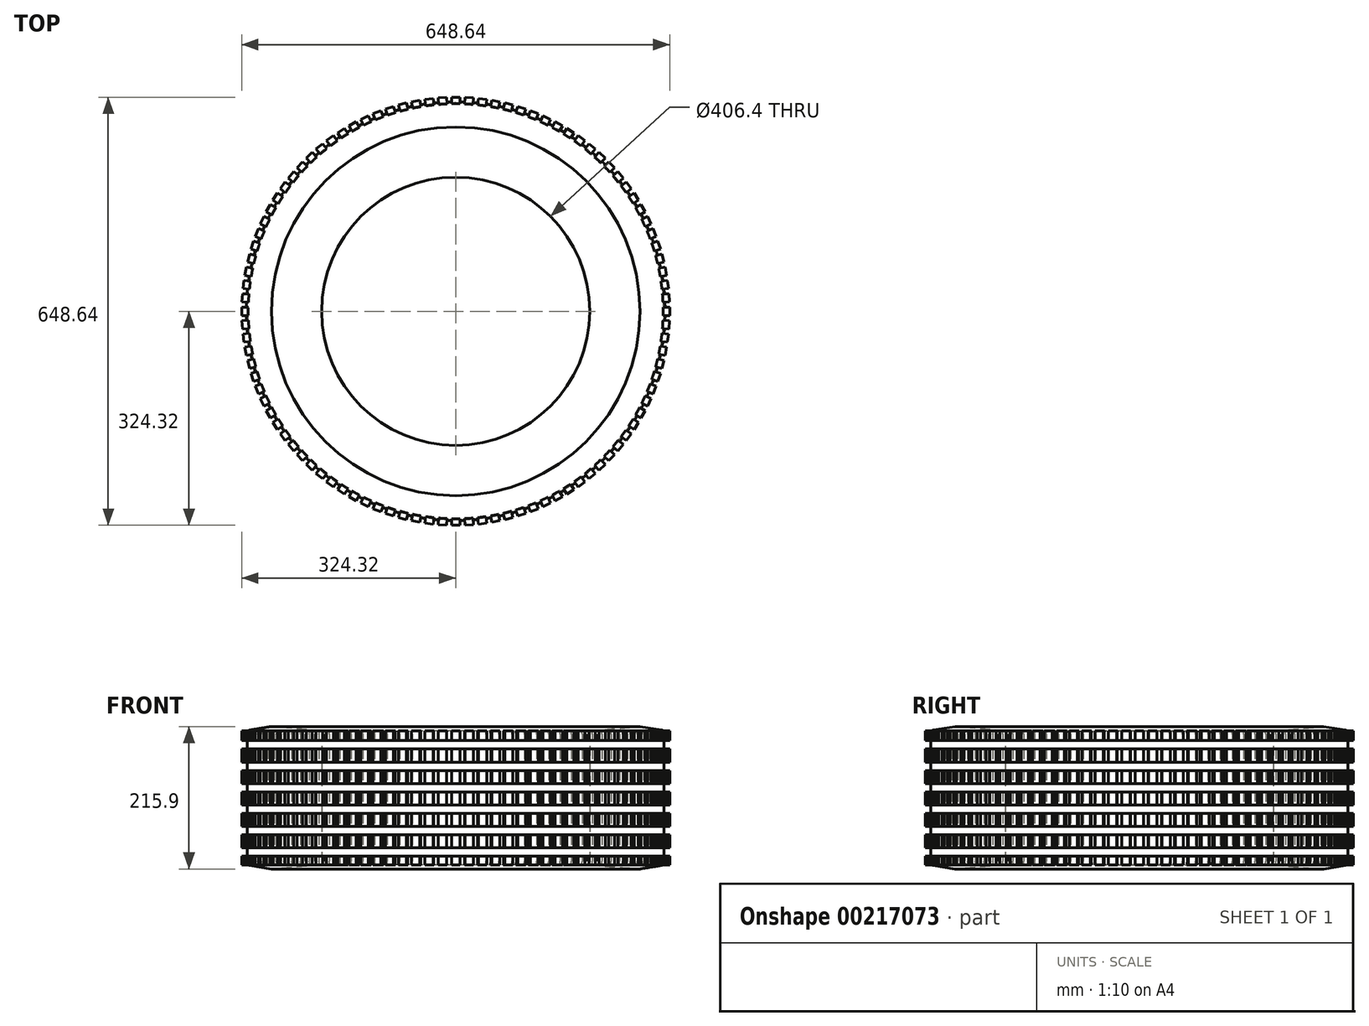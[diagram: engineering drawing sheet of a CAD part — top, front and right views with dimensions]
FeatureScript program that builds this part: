
annotation { "Feature Type Name" : "Feature", "Feature Type Description" : "" }
export const myFeature = defineFeature(function(context is Context, id is Id, definition is map)
    precondition{}
    {
        {
            var Q0;
            Q0=qCreatedBy(makeId("Top.planeOp"),FACE);
            var sketch = newSketch(context, id + "F0", { "sketchPlane" : qUnion([Q0])});
            skCircle(sketch, "E0", {"center": v(0, 0) * mm, "radius": 317.5 * mm});
            skCircle(sketch, "E1", {"center": v(0, 0) * mm, "radius": 203.2 * mm});
            skLineSegment(sketch, "E2", {"start": v(0, 0) * mm, "end": v(0, 317.5) * mm});
            skSolve(sketch);
        }
        {
            var Q0;
            Q0 = qSketchRegion(id + "F0", true);
            extrude(context, id + "F1", {"entities" : qUnion([Q0]), "depth" : 209.55 * mm, "hasSecondDirection" : true, "secondDirectionOppositeDirection" : true, "secondDirectionDepth" : 6.35 * mm});
        }
        {
            var Q0;
            Q0=makeQuery(id+"F1.opExtrude","CAP_EDGE",EDGE,{"disambiguationData":[OSD([sQuery(id+"F0.wireOp",EDGE,"E0")])],"isStart":true});
            chamfer(context, id + "F2", {"entities" : qUnion([Q0]), "chamferType" : ChamferType.TWO_OFFSETS, "width1" : 6.35 * mm, "oppositeDirection" : false, "width2" : 38.1 * mm, "tangentPropagation" : true});
        }
        {
            var Q0;
            Q0=makeQuery(id+"F1.opExtrude","CAP_EDGE",EDGE,{"disambiguationData":[OSD([sQuery(id+"F0.wireOp",EDGE,"E0")])],"isStart":false});
            chamfer(context, id + "F3", {"entities" : qUnion([Q0]), "chamferType" : ChamferType.TWO_OFFSETS, "width1" : 6.35 * mm, "oppositeDirection" : true, "width2" : 38.1 * mm, "tangentPropagation" : true});
        }
        {
            var Q0;
            Q0=makeQuery(id+"F1.opExtrude","CAP_EDGE",EDGE,{"disambiguationData":[OSD([sQuery(id+"F0.wireOp",EDGE,"E1")])],"isStart":true});
            chamfer(context, id + "F4", {"entities" : qUnion([Q0]), "chamferType" : ChamferType.TWO_OFFSETS, "width1" : 76.2 * mm, "oppositeDirection" : false, "width2" : 6.35 * mm, "tangentPropagation" : true});
        }
        {
            var Q0;
            Q0=makeQuery(id+"F1.opExtrude","CAP_EDGE",EDGE,{"disambiguationData":[OSD([sQuery(id+"F0.wireOp",EDGE,"E1")])],"isStart":false});
            chamfer(context, id + "F5", {"entities" : qUnion([Q0]), "chamferType" : ChamferType.TWO_OFFSETS, "width1" : 6.35 * mm, "oppositeDirection" : false, "width2" : 76.2 * mm, "tangentPropagation" : true});
        }
        {
            var Q0;
            {var subQ0=sQuery(id+"F0.wireOp",EDGE,"E0");Q0=makeQuery(id+"F2.opChamfer","BLEND_EDGE",EDGE,{"blendedFrom":[makeQuery(id+"F1.opExtrude","CAP_EDGE",EDGE,{"disambiguationData":[OSD([subQ0])],"isStart":true}),makeQuery(id+"F1.opExtrude","SWEPT_FACE",FACE,{"disambiguationData":[OSD([subQ0])]})],"blendedInto":[makeQuery(id+"F1.opExtrude","SWEPT_FACE",FACE,{"disambiguationData":[OSD([subQ0])]})]});}
            var Q1;
            {var subQ0=sQuery(id+"F0.wireOp",EDGE,"E0");Q1=makeQuery(id+"F3.opChamfer","BLEND_EDGE",EDGE,{"blendedFrom":[makeQuery(id+"F1.opExtrude","CAP_EDGE",EDGE,{"disambiguationData":[OSD([subQ0])],"isStart":false}),makeQuery(id+"F1.opExtrude","SWEPT_FACE",FACE,{"disambiguationData":[OSD([subQ0])]})],"blendedInto":[makeQuery(id+"F1.opExtrude","SWEPT_FACE",FACE,{"disambiguationData":[OSD([subQ0])]})]});}
            fillet(context, id + "F6", {"entities" : qUnion([Q0, Q1]), "radius" : 6.35 * mm, "tangentPropagation" : true, "allowEdgeOverflow" : false});
        }
        {
            var Q0;
            Q0=qCreatedBy(makeId("Top.planeOp"),FACE);
            var sketch = newSketch(context, id + "F7", { "sketchPlane" : qUnion([Q0])});
            skLineSegment(sketch, "E3.bottom", {"start": v(6.35, -311.62) * mm, "end": v(-6.35, -311.62) * mm});
            skLineSegment(sketch, "E3.top", {"start": v(6.35, -324.32) * mm, "end": v(-6.35, -324.32) * mm});
            skLineSegment(sketch, "E3.left", {"start": v(6.35, -311.62) * mm, "end": v(6.35, -324.32) * mm});
            skLineSegment(sketch, "E3.right", {"start": v(-6.35, -311.62) * mm, "end": v(-6.35, -324.32) * mm});
            skPoint(sketch, "E3.middle", {"position": v(0, -317.97) * mm});
            skLineSegment(sketch, "E4.1.0", {"start": v(13.23, -311.4) * mm, "end": v(14.03, -324.08) * mm});
            skLineSegment(sketch, "E4.1.1", {"start": v(25.9, -310.61) * mm, "end": v(26.7, -323.29) * mm});
            skLineSegment(sketch, "E4.1.2", {"start": v(26.7, -323.29) * mm, "end": v(14.03, -324.08) * mm});
            skLineSegment(sketch, "E4.1.3", {"start": v(25.9, -310.61) * mm, "end": v(13.23, -311.4) * mm});
            skLineSegment(sketch, "E4.2.0", {"start": v(32.76, -309.96) * mm, "end": v(34.35, -322.56) * mm});
            skLineSegment(sketch, "E4.2.1", {"start": v(45.36, -308.37) * mm, "end": v(46.95, -320.97) * mm});
            skLineSegment(sketch, "E4.2.2", {"start": v(46.95, -320.97) * mm, "end": v(34.35, -322.56) * mm});
            skLineSegment(sketch, "E4.2.3", {"start": v(45.36, -308.37) * mm, "end": v(32.76, -309.96) * mm});
            skLineSegment(sketch, "E4.3.0", {"start": v(52.15, -307.3) * mm, "end": v(54.53, -319.77) * mm});
            skLineSegment(sketch, "E4.3.1", {"start": v(64.63, -304.91) * mm, "end": v(67, -317.39) * mm});
            skLineSegment(sketch, "E4.3.2", {"start": v(67, -317.39) * mm, "end": v(54.53, -319.77) * mm});
            skLineSegment(sketch, "E4.3.3", {"start": v(64.63, -304.91) * mm, "end": v(52.15, -307.3) * mm});
            skLineSegment(sketch, "E4.4.0", {"start": v(71.35, -303.41) * mm, "end": v(74.5, -315.71) * mm});
            skLineSegment(sketch, "E4.4.1", {"start": v(83.65, -300.25) * mm, "end": v(86.8, -312.56) * mm});
            skLineSegment(sketch, "E4.4.2", {"start": v(86.8, -312.56) * mm, "end": v(74.5, -315.71) * mm});
            skLineSegment(sketch, "E4.4.3", {"start": v(83.65, -300.25) * mm, "end": v(71.35, -303.41) * mm});
            skLineSegment(sketch, "E4.5.0", {"start": v(90.26, -298.33) * mm, "end": v(94.18, -310.41) * mm});
            skLineSegment(sketch, "E4.5.1", {"start": v(102.34, -294.4) * mm, "end": v(106.26, -306.49) * mm});
            skLineSegment(sketch, "E4.5.2", {"start": v(106.26, -306.49) * mm, "end": v(94.18, -310.41) * mm});
            skLineSegment(sketch, "E4.5.3", {"start": v(102.34, -294.4) * mm, "end": v(90.26, -298.33) * mm});
            skLineSegment(sketch, "E4.6.0", {"start": v(108.81, -292.08) * mm, "end": v(113.49, -303.89) * mm});
            skLineSegment(sketch, "E4.6.1", {"start": v(120.62, -287.4) * mm, "end": v(125.3, -299.21) * mm});
            skLineSegment(sketch, "E4.6.2", {"start": v(125.3, -299.21) * mm, "end": v(113.49, -303.89) * mm});
            skLineSegment(sketch, "E4.6.3", {"start": v(120.62, -287.4) * mm, "end": v(108.81, -292.08) * mm});
            skLineSegment(sketch, "E4.7.0", {"start": v(126.94, -284.67) * mm, "end": v(132.34, -296.16) * mm});
            skLineSegment(sketch, "E4.7.1", {"start": v(138.43, -279.26) * mm, "end": v(143.84, -290.75) * mm});
            skLineSegment(sketch, "E4.7.2", {"start": v(143.84, -290.75) * mm, "end": v(132.34, -296.16) * mm});
            skLineSegment(sketch, "E4.7.3", {"start": v(138.43, -279.26) * mm, "end": v(126.94, -284.67) * mm});
            skLineSegment(sketch, "E4.8.0", {"start": v(144.56, -276.14) * mm, "end": v(150.68, -287.27) * mm});
            skLineSegment(sketch, "E4.8.1", {"start": v(155.7, -270.02) * mm, "end": v(161.8, -281.15) * mm});
            skLineSegment(sketch, "E4.8.2", {"start": v(161.8, -281.15) * mm, "end": v(150.68, -287.27) * mm});
            skLineSegment(sketch, "E4.8.3", {"start": v(155.7, -270.02) * mm, "end": v(144.56, -276.14) * mm});
            skLineSegment(sketch, "E4.9.0", {"start": v(161.61, -266.52) * mm, "end": v(168.42, -277.24) * mm});
            skLineSegment(sketch, "E4.9.1", {"start": v(172.34, -259.71) * mm, "end": v(179.14, -270.43) * mm});
            skLineSegment(sketch, "E4.9.2", {"start": v(179.14, -270.43) * mm, "end": v(168.42, -277.24) * mm});
            skLineSegment(sketch, "E4.9.3", {"start": v(172.34, -259.71) * mm, "end": v(161.61, -266.52) * mm});
            skLineSegment(sketch, "E4.10.0", {"start": v(178.03, -255.84) * mm, "end": v(185.5, -266.12) * mm});
            skLineSegment(sketch, "E4.10.1", {"start": v(188.3, -248.38) * mm, "end": v(195.77, -258.65) * mm});
            skLineSegment(sketch, "E4.10.2", {"start": v(195.77, -258.65) * mm, "end": v(185.5, -266.12) * mm});
            skLineSegment(sketch, "E4.10.3", {"start": v(188.3, -248.38) * mm, "end": v(178.03, -255.84) * mm});
            skLineSegment(sketch, "E4.11.0", {"start": v(193.74, -244.16) * mm, "end": v(201.84, -253.94) * mm});
            skLineSegment(sketch, "E4.11.1", {"start": v(203.53, -236.06) * mm, "end": v(211.62, -245.85) * mm});
            skLineSegment(sketch, "E4.11.2", {"start": v(211.62, -245.85) * mm, "end": v(201.84, -253.94) * mm});
            skLineSegment(sketch, "E4.11.3", {"start": v(203.53, -236.06) * mm, "end": v(193.74, -244.16) * mm});
            skLineSegment(sketch, "E4.12.0", {"start": v(208.7, -231.51) * mm, "end": v(217.39, -240.77) * mm});
            skLineSegment(sketch, "E4.12.1", {"start": v(217.95, -222.82) * mm, "end": v(226.64, -232.08) * mm});
            skLineSegment(sketch, "E4.12.2", {"start": v(226.64, -232.08) * mm, "end": v(217.39, -240.77) * mm});
            skLineSegment(sketch, "E4.12.3", {"start": v(217.95, -222.82) * mm, "end": v(208.7, -231.51) * mm});
            skLineSegment(sketch, "E4.13.0", {"start": v(222.82, -217.95) * mm, "end": v(232.08, -226.64) * mm});
            skLineSegment(sketch, "E4.13.1", {"start": v(231.51, -208.7) * mm, "end": v(240.77, -217.39) * mm});
            skLineSegment(sketch, "E4.13.2", {"start": v(240.77, -217.39) * mm, "end": v(232.08, -226.64) * mm});
            skLineSegment(sketch, "E4.13.3", {"start": v(231.51, -208.7) * mm, "end": v(222.82, -217.95) * mm});
            skLineSegment(sketch, "E4.14.0", {"start": v(236.06, -203.53) * mm, "end": v(245.85, -211.62) * mm});
            skLineSegment(sketch, "E4.14.1", {"start": v(244.16, -193.74) * mm, "end": v(253.94, -201.84) * mm});
            skLineSegment(sketch, "E4.14.2", {"start": v(253.94, -201.84) * mm, "end": v(245.85, -211.62) * mm});
            skLineSegment(sketch, "E4.14.3", {"start": v(244.16, -193.74) * mm, "end": v(236.06, -203.53) * mm});
            skLineSegment(sketch, "E4.15.0", {"start": v(248.38, -188.3) * mm, "end": v(258.65, -195.77) * mm});
            skLineSegment(sketch, "E4.15.1", {"start": v(255.84, -178.03) * mm, "end": v(266.12, -185.5) * mm});
            skLineSegment(sketch, "E4.15.2", {"start": v(266.12, -185.5) * mm, "end": v(258.65, -195.77) * mm});
            skLineSegment(sketch, "E4.15.3", {"start": v(255.84, -178.03) * mm, "end": v(248.38, -188.3) * mm});
            skLineSegment(sketch, "E4.16.0", {"start": v(259.71, -172.34) * mm, "end": v(270.43, -179.14) * mm});
            skLineSegment(sketch, "E4.16.1", {"start": v(266.52, -161.61) * mm, "end": v(277.24, -168.42) * mm});
            skLineSegment(sketch, "E4.16.2", {"start": v(277.24, -168.42) * mm, "end": v(270.43, -179.14) * mm});
            skLineSegment(sketch, "E4.16.3", {"start": v(266.52, -161.61) * mm, "end": v(259.71, -172.34) * mm});
            skLineSegment(sketch, "E4.17.0", {"start": v(270.02, -155.7) * mm, "end": v(281.15, -161.8) * mm});
            skLineSegment(sketch, "E4.17.1", {"start": v(276.14, -144.56) * mm, "end": v(287.27, -150.68) * mm});
            skLineSegment(sketch, "E4.17.2", {"start": v(287.27, -150.68) * mm, "end": v(281.15, -161.8) * mm});
            skLineSegment(sketch, "E4.17.3", {"start": v(276.14, -144.56) * mm, "end": v(270.02, -155.7) * mm});
            skLineSegment(sketch, "E4.18.0", {"start": v(279.26, -138.43) * mm, "end": v(290.75, -143.84) * mm});
            skLineSegment(sketch, "E4.18.1", {"start": v(284.67, -126.94) * mm, "end": v(296.16, -132.34) * mm});
            skLineSegment(sketch, "E4.18.2", {"start": v(296.16, -132.34) * mm, "end": v(290.75, -143.84) * mm});
            skLineSegment(sketch, "E4.18.3", {"start": v(284.67, -126.94) * mm, "end": v(279.26, -138.43) * mm});
            skLineSegment(sketch, "E4.19.0", {"start": v(287.4, -120.62) * mm, "end": v(299.21, -125.3) * mm});
            skLineSegment(sketch, "E4.19.1", {"start": v(292.08, -108.81) * mm, "end": v(303.89, -113.49) * mm});
            skLineSegment(sketch, "E4.19.2", {"start": v(303.89, -113.49) * mm, "end": v(299.21, -125.3) * mm});
            skLineSegment(sketch, "E4.19.3", {"start": v(292.08, -108.81) * mm, "end": v(287.4, -120.62) * mm});
            skLineSegment(sketch, "E4.20.0", {"start": v(294.4, -102.34) * mm, "end": v(306.49, -106.26) * mm});
            skLineSegment(sketch, "E4.20.1", {"start": v(298.33, -90.26) * mm, "end": v(310.41, -94.18) * mm});
            skLineSegment(sketch, "E4.20.2", {"start": v(310.41, -94.18) * mm, "end": v(306.49, -106.26) * mm});
            skLineSegment(sketch, "E4.20.3", {"start": v(298.33, -90.26) * mm, "end": v(294.4, -102.34) * mm});
            skLineSegment(sketch, "E4.21.0", {"start": v(300.25, -83.65) * mm, "end": v(312.56, -86.8) * mm});
            skLineSegment(sketch, "E4.21.1", {"start": v(303.41, -71.35) * mm, "end": v(315.71, -74.5) * mm});
            skLineSegment(sketch, "E4.21.2", {"start": v(315.71, -74.5) * mm, "end": v(312.56, -86.8) * mm});
            skLineSegment(sketch, "E4.21.3", {"start": v(303.41, -71.35) * mm, "end": v(300.25, -83.65) * mm});
            skLineSegment(sketch, "E4.22.0", {"start": v(304.91, -64.63) * mm, "end": v(317.39, -67) * mm});
            skLineSegment(sketch, "E4.22.1", {"start": v(307.3, -52.15) * mm, "end": v(319.77, -54.53) * mm});
            skLineSegment(sketch, "E4.22.2", {"start": v(319.77, -54.53) * mm, "end": v(317.39, -67) * mm});
            skLineSegment(sketch, "E4.22.3", {"start": v(307.3, -52.15) * mm, "end": v(304.91, -64.63) * mm});
            skLineSegment(sketch, "E4.23.0", {"start": v(308.37, -45.36) * mm, "end": v(320.97, -46.95) * mm});
            skLineSegment(sketch, "E4.23.1", {"start": v(309.96, -32.76) * mm, "end": v(322.56, -34.35) * mm});
            skLineSegment(sketch, "E4.23.2", {"start": v(322.56, -34.35) * mm, "end": v(320.97, -46.95) * mm});
            skLineSegment(sketch, "E4.23.3", {"start": v(309.96, -32.76) * mm, "end": v(308.37, -45.36) * mm});
            skLineSegment(sketch, "E4.24.0", {"start": v(310.61, -25.9) * mm, "end": v(323.29, -26.7) * mm});
            skLineSegment(sketch, "E4.24.1", {"start": v(311.4, -13.23) * mm, "end": v(324.08, -14.03) * mm});
            skLineSegment(sketch, "E4.24.2", {"start": v(324.08, -14.03) * mm, "end": v(323.29, -26.7) * mm});
            skLineSegment(sketch, "E4.24.3", {"start": v(311.4, -13.23) * mm, "end": v(310.61, -25.9) * mm});
            skLineSegment(sketch, "E4.25.0", {"start": v(311.62, -6.35) * mm, "end": v(324.32, -6.35) * mm});
            skLineSegment(sketch, "E4.25.1", {"start": v(311.62, 6.35) * mm, "end": v(324.32, 6.35) * mm});
            skLineSegment(sketch, "E4.25.2", {"start": v(324.32, 6.35) * mm, "end": v(324.32, -6.35) * mm});
            skLineSegment(sketch, "E4.25.3", {"start": v(311.62, 6.35) * mm, "end": v(311.62, -6.35) * mm});
            skLineSegment(sketch, "E4.26.0", {"start": v(311.4, 13.23) * mm, "end": v(324.08, 14.03) * mm});
            skLineSegment(sketch, "E4.26.1", {"start": v(310.61, 25.9) * mm, "end": v(323.29, 26.7) * mm});
            skLineSegment(sketch, "E4.26.2", {"start": v(323.29, 26.7) * mm, "end": v(324.08, 14.03) * mm});
            skLineSegment(sketch, "E4.26.3", {"start": v(310.61, 25.9) * mm, "end": v(311.4, 13.23) * mm});
            skLineSegment(sketch, "E4.27.0", {"start": v(309.96, 32.76) * mm, "end": v(322.56, 34.35) * mm});
            skLineSegment(sketch, "E4.27.1", {"start": v(308.37, 45.36) * mm, "end": v(320.97, 46.95) * mm});
            skLineSegment(sketch, "E4.27.2", {"start": v(320.97, 46.95) * mm, "end": v(322.56, 34.35) * mm});
            skLineSegment(sketch, "E4.27.3", {"start": v(308.37, 45.36) * mm, "end": v(309.96, 32.76) * mm});
            skLineSegment(sketch, "E4.28.0", {"start": v(307.3, 52.15) * mm, "end": v(319.77, 54.53) * mm});
            skLineSegment(sketch, "E4.28.1", {"start": v(304.91, 64.63) * mm, "end": v(317.39, 67) * mm});
            skLineSegment(sketch, "E4.28.2", {"start": v(317.39, 67) * mm, "end": v(319.77, 54.53) * mm});
            skLineSegment(sketch, "E4.28.3", {"start": v(304.91, 64.63) * mm, "end": v(307.3, 52.15) * mm});
            skLineSegment(sketch, "E4.29.0", {"start": v(303.41, 71.35) * mm, "end": v(315.71, 74.5) * mm});
            skLineSegment(sketch, "E4.29.1", {"start": v(300.25, 83.65) * mm, "end": v(312.56, 86.8) * mm});
            skLineSegment(sketch, "E4.29.2", {"start": v(312.56, 86.8) * mm, "end": v(315.71, 74.5) * mm});
            skLineSegment(sketch, "E4.29.3", {"start": v(300.25, 83.65) * mm, "end": v(303.41, 71.35) * mm});
            skLineSegment(sketch, "E4.30.0", {"start": v(298.33, 90.26) * mm, "end": v(310.41, 94.18) * mm});
            skLineSegment(sketch, "E4.30.1", {"start": v(294.4, 102.34) * mm, "end": v(306.49, 106.26) * mm});
            skLineSegment(sketch, "E4.30.2", {"start": v(306.49, 106.26) * mm, "end": v(310.41, 94.18) * mm});
            skLineSegment(sketch, "E4.30.3", {"start": v(294.4, 102.34) * mm, "end": v(298.33, 90.26) * mm});
            skLineSegment(sketch, "E4.31.0", {"start": v(292.08, 108.81) * mm, "end": v(303.89, 113.49) * mm});
            skLineSegment(sketch, "E4.31.1", {"start": v(287.4, 120.62) * mm, "end": v(299.21, 125.3) * mm});
            skLineSegment(sketch, "E4.31.2", {"start": v(299.21, 125.3) * mm, "end": v(303.89, 113.49) * mm});
            skLineSegment(sketch, "E4.31.3", {"start": v(287.4, 120.62) * mm, "end": v(292.08, 108.81) * mm});
            skLineSegment(sketch, "E4.32.0", {"start": v(284.67, 126.94) * mm, "end": v(296.16, 132.34) * mm});
            skLineSegment(sketch, "E4.32.1", {"start": v(279.26, 138.43) * mm, "end": v(290.75, 143.84) * mm});
            skLineSegment(sketch, "E4.32.2", {"start": v(290.75, 143.84) * mm, "end": v(296.16, 132.34) * mm});
            skLineSegment(sketch, "E4.32.3", {"start": v(279.26, 138.43) * mm, "end": v(284.67, 126.94) * mm});
            skLineSegment(sketch, "E4.33.0", {"start": v(276.14, 144.56) * mm, "end": v(287.27, 150.68) * mm});
            skLineSegment(sketch, "E4.33.1", {"start": v(270.02, 155.7) * mm, "end": v(281.15, 161.8) * mm});
            skLineSegment(sketch, "E4.33.2", {"start": v(281.15, 161.8) * mm, "end": v(287.27, 150.68) * mm});
            skLineSegment(sketch, "E4.33.3", {"start": v(270.02, 155.7) * mm, "end": v(276.14, 144.56) * mm});
            skLineSegment(sketch, "E4.34.0", {"start": v(266.52, 161.61) * mm, "end": v(277.24, 168.42) * mm});
            skLineSegment(sketch, "E4.34.1", {"start": v(259.71, 172.34) * mm, "end": v(270.43, 179.14) * mm});
            skLineSegment(sketch, "E4.34.2", {"start": v(270.43, 179.14) * mm, "end": v(277.24, 168.42) * mm});
            skLineSegment(sketch, "E4.34.3", {"start": v(259.71, 172.34) * mm, "end": v(266.52, 161.61) * mm});
            skLineSegment(sketch, "E4.35.0", {"start": v(255.84, 178.03) * mm, "end": v(266.12, 185.5) * mm});
            skLineSegment(sketch, "E4.35.1", {"start": v(248.38, 188.3) * mm, "end": v(258.65, 195.77) * mm});
            skLineSegment(sketch, "E4.35.2", {"start": v(258.65, 195.77) * mm, "end": v(266.12, 185.5) * mm});
            skLineSegment(sketch, "E4.35.3", {"start": v(248.38, 188.3) * mm, "end": v(255.84, 178.03) * mm});
            skLineSegment(sketch, "E4.36.0", {"start": v(244.16, 193.74) * mm, "end": v(253.94, 201.84) * mm});
            skLineSegment(sketch, "E4.36.1", {"start": v(236.06, 203.53) * mm, "end": v(245.85, 211.62) * mm});
            skLineSegment(sketch, "E4.36.2", {"start": v(245.85, 211.62) * mm, "end": v(253.94, 201.84) * mm});
            skLineSegment(sketch, "E4.36.3", {"start": v(236.06, 203.53) * mm, "end": v(244.16, 193.74) * mm});
            skLineSegment(sketch, "E4.37.0", {"start": v(231.51, 208.7) * mm, "end": v(240.77, 217.39) * mm});
            skLineSegment(sketch, "E4.37.1", {"start": v(222.82, 217.95) * mm, "end": v(232.08, 226.64) * mm});
            skLineSegment(sketch, "E4.37.2", {"start": v(232.08, 226.64) * mm, "end": v(240.77, 217.39) * mm});
            skLineSegment(sketch, "E4.37.3", {"start": v(222.82, 217.95) * mm, "end": v(231.51, 208.7) * mm});
            skLineSegment(sketch, "E4.38.0", {"start": v(217.95, 222.82) * mm, "end": v(226.64, 232.08) * mm});
            skLineSegment(sketch, "E4.38.1", {"start": v(208.7, 231.51) * mm, "end": v(217.39, 240.77) * mm});
            skLineSegment(sketch, "E4.38.2", {"start": v(217.39, 240.77) * mm, "end": v(226.64, 232.08) * mm});
            skLineSegment(sketch, "E4.38.3", {"start": v(208.7, 231.51) * mm, "end": v(217.95, 222.82) * mm});
            skLineSegment(sketch, "E4.39.0", {"start": v(203.53, 236.06) * mm, "end": v(211.62, 245.85) * mm});
            skLineSegment(sketch, "E4.39.1", {"start": v(193.74, 244.16) * mm, "end": v(201.84, 253.94) * mm});
            skLineSegment(sketch, "E4.39.2", {"start": v(201.84, 253.94) * mm, "end": v(211.62, 245.85) * mm});
            skLineSegment(sketch, "E4.39.3", {"start": v(193.74, 244.16) * mm, "end": v(203.53, 236.06) * mm});
            skLineSegment(sketch, "E4.40.0", {"start": v(188.3, 248.38) * mm, "end": v(195.77, 258.65) * mm});
            skLineSegment(sketch, "E4.40.1", {"start": v(178.03, 255.84) * mm, "end": v(185.5, 266.12) * mm});
            skLineSegment(sketch, "E4.40.2", {"start": v(185.5, 266.12) * mm, "end": v(195.77, 258.65) * mm});
            skLineSegment(sketch, "E4.40.3", {"start": v(178.03, 255.84) * mm, "end": v(188.3, 248.38) * mm});
            skLineSegment(sketch, "E4.41.0", {"start": v(172.34, 259.71) * mm, "end": v(179.14, 270.43) * mm});
            skLineSegment(sketch, "E4.41.1", {"start": v(161.61, 266.52) * mm, "end": v(168.42, 277.24) * mm});
            skLineSegment(sketch, "E4.41.2", {"start": v(168.42, 277.24) * mm, "end": v(179.14, 270.43) * mm});
            skLineSegment(sketch, "E4.41.3", {"start": v(161.61, 266.52) * mm, "end": v(172.34, 259.71) * mm});
            skLineSegment(sketch, "E4.42.0", {"start": v(155.7, 270.02) * mm, "end": v(161.8, 281.15) * mm});
            skLineSegment(sketch, "E4.42.1", {"start": v(144.56, 276.14) * mm, "end": v(150.68, 287.27) * mm});
            skLineSegment(sketch, "E4.42.2", {"start": v(150.68, 287.27) * mm, "end": v(161.8, 281.15) * mm});
            skLineSegment(sketch, "E4.42.3", {"start": v(144.56, 276.14) * mm, "end": v(155.7, 270.02) * mm});
            skLineSegment(sketch, "E4.43.0", {"start": v(138.43, 279.26) * mm, "end": v(143.84, 290.75) * mm});
            skLineSegment(sketch, "E4.43.1", {"start": v(126.94, 284.67) * mm, "end": v(132.34, 296.16) * mm});
            skLineSegment(sketch, "E4.43.2", {"start": v(132.34, 296.16) * mm, "end": v(143.84, 290.75) * mm});
            skLineSegment(sketch, "E4.43.3", {"start": v(126.94, 284.67) * mm, "end": v(138.43, 279.26) * mm});
            skLineSegment(sketch, "E4.44.0", {"start": v(120.62, 287.4) * mm, "end": v(125.3, 299.21) * mm});
            skLineSegment(sketch, "E4.44.1", {"start": v(108.81, 292.08) * mm, "end": v(113.49, 303.89) * mm});
            skLineSegment(sketch, "E4.44.2", {"start": v(113.49, 303.89) * mm, "end": v(125.3, 299.21) * mm});
            skLineSegment(sketch, "E4.44.3", {"start": v(108.81, 292.08) * mm, "end": v(120.62, 287.4) * mm});
            skLineSegment(sketch, "E4.45.0", {"start": v(102.34, 294.4) * mm, "end": v(106.26, 306.49) * mm});
            skLineSegment(sketch, "E4.45.1", {"start": v(90.26, 298.33) * mm, "end": v(94.18, 310.41) * mm});
            skLineSegment(sketch, "E4.45.2", {"start": v(94.18, 310.41) * mm, "end": v(106.26, 306.49) * mm});
            skLineSegment(sketch, "E4.45.3", {"start": v(90.26, 298.33) * mm, "end": v(102.34, 294.4) * mm});
            skLineSegment(sketch, "E4.46.0", {"start": v(83.65, 300.25) * mm, "end": v(86.8, 312.56) * mm});
            skLineSegment(sketch, "E4.46.1", {"start": v(71.35, 303.41) * mm, "end": v(74.5, 315.71) * mm});
            skLineSegment(sketch, "E4.46.2", {"start": v(74.5, 315.71) * mm, "end": v(86.8, 312.56) * mm});
            skLineSegment(sketch, "E4.46.3", {"start": v(71.35, 303.41) * mm, "end": v(83.65, 300.25) * mm});
            skLineSegment(sketch, "E4.47.0", {"start": v(64.63, 304.91) * mm, "end": v(67, 317.39) * mm});
            skLineSegment(sketch, "E4.47.1", {"start": v(52.15, 307.3) * mm, "end": v(54.53, 319.77) * mm});
            skLineSegment(sketch, "E4.47.2", {"start": v(54.53, 319.77) * mm, "end": v(67, 317.39) * mm});
            skLineSegment(sketch, "E4.47.3", {"start": v(52.15, 307.3) * mm, "end": v(64.63, 304.91) * mm});
            skLineSegment(sketch, "E4.48.0", {"start": v(45.36, 308.37) * mm, "end": v(46.95, 320.97) * mm});
            skLineSegment(sketch, "E4.48.1", {"start": v(32.76, 309.96) * mm, "end": v(34.35, 322.56) * mm});
            skLineSegment(sketch, "E4.48.2", {"start": v(34.35, 322.56) * mm, "end": v(46.95, 320.97) * mm});
            skLineSegment(sketch, "E4.48.3", {"start": v(32.76, 309.96) * mm, "end": v(45.36, 308.37) * mm});
            skLineSegment(sketch, "E4.49.0", {"start": v(25.9, 310.61) * mm, "end": v(26.7, 323.29) * mm});
            skLineSegment(sketch, "E4.49.1", {"start": v(13.23, 311.4) * mm, "end": v(14.03, 324.08) * mm});
            skLineSegment(sketch, "E4.49.2", {"start": v(14.03, 324.08) * mm, "end": v(26.7, 323.29) * mm});
            skLineSegment(sketch, "E4.49.3", {"start": v(13.23, 311.4) * mm, "end": v(25.9, 310.61) * mm});
            skLineSegment(sketch, "E4.50.0", {"start": v(6.35, 311.62) * mm, "end": v(6.35, 324.32) * mm});
            skLineSegment(sketch, "E4.50.1", {"start": v(-6.35, 311.62) * mm, "end": v(-6.35, 324.32) * mm});
            skLineSegment(sketch, "E4.50.2", {"start": v(-6.35, 324.32) * mm, "end": v(6.35, 324.32) * mm});
            skLineSegment(sketch, "E4.50.3", {"start": v(-6.35, 311.62) * mm, "end": v(6.35, 311.62) * mm});
            skLineSegment(sketch, "E4.51.0", {"start": v(-13.23, 311.4) * mm, "end": v(-14.03, 324.08) * mm});
            skLineSegment(sketch, "E4.51.1", {"start": v(-25.9, 310.61) * mm, "end": v(-26.7, 323.29) * mm});
            skLineSegment(sketch, "E4.51.2", {"start": v(-26.7, 323.29) * mm, "end": v(-14.03, 324.08) * mm});
            skLineSegment(sketch, "E4.51.3", {"start": v(-25.9, 310.61) * mm, "end": v(-13.23, 311.4) * mm});
            skLineSegment(sketch, "E4.52.0", {"start": v(-32.76, 309.96) * mm, "end": v(-34.35, 322.56) * mm});
            skLineSegment(sketch, "E4.52.1", {"start": v(-45.36, 308.37) * mm, "end": v(-46.95, 320.97) * mm});
            skLineSegment(sketch, "E4.52.2", {"start": v(-46.95, 320.97) * mm, "end": v(-34.35, 322.56) * mm});
            skLineSegment(sketch, "E4.52.3", {"start": v(-45.36, 308.37) * mm, "end": v(-32.76, 309.96) * mm});
            skLineSegment(sketch, "E4.53.0", {"start": v(-52.15, 307.3) * mm, "end": v(-54.53, 319.77) * mm});
            skLineSegment(sketch, "E4.53.1", {"start": v(-64.63, 304.91) * mm, "end": v(-67, 317.39) * mm});
            skLineSegment(sketch, "E4.53.2", {"start": v(-67, 317.39) * mm, "end": v(-54.53, 319.77) * mm});
            skLineSegment(sketch, "E4.53.3", {"start": v(-64.63, 304.91) * mm, "end": v(-52.15, 307.3) * mm});
            skLineSegment(sketch, "E4.54.0", {"start": v(-71.35, 303.41) * mm, "end": v(-74.5, 315.71) * mm});
            skLineSegment(sketch, "E4.54.1", {"start": v(-83.65, 300.25) * mm, "end": v(-86.8, 312.56) * mm});
            skLineSegment(sketch, "E4.54.2", {"start": v(-86.8, 312.56) * mm, "end": v(-74.5, 315.71) * mm});
            skLineSegment(sketch, "E4.54.3", {"start": v(-83.65, 300.25) * mm, "end": v(-71.35, 303.41) * mm});
            skLineSegment(sketch, "E4.55.0", {"start": v(-90.26, 298.33) * mm, "end": v(-94.18, 310.41) * mm});
            skLineSegment(sketch, "E4.55.1", {"start": v(-102.34, 294.4) * mm, "end": v(-106.26, 306.49) * mm});
            skLineSegment(sketch, "E4.55.2", {"start": v(-106.26, 306.49) * mm, "end": v(-94.18, 310.41) * mm});
            skLineSegment(sketch, "E4.55.3", {"start": v(-102.34, 294.4) * mm, "end": v(-90.26, 298.33) * mm});
            skLineSegment(sketch, "E4.56.0", {"start": v(-108.81, 292.08) * mm, "end": v(-113.49, 303.89) * mm});
            skLineSegment(sketch, "E4.56.1", {"start": v(-120.62, 287.4) * mm, "end": v(-125.3, 299.21) * mm});
            skLineSegment(sketch, "E4.56.2", {"start": v(-125.3, 299.21) * mm, "end": v(-113.49, 303.89) * mm});
            skLineSegment(sketch, "E4.56.3", {"start": v(-120.62, 287.4) * mm, "end": v(-108.81, 292.08) * mm});
            skLineSegment(sketch, "E4.57.0", {"start": v(-126.94, 284.67) * mm, "end": v(-132.34, 296.16) * mm});
            skLineSegment(sketch, "E4.57.1", {"start": v(-138.43, 279.26) * mm, "end": v(-143.84, 290.75) * mm});
            skLineSegment(sketch, "E4.57.2", {"start": v(-143.84, 290.75) * mm, "end": v(-132.34, 296.16) * mm});
            skLineSegment(sketch, "E4.57.3", {"start": v(-138.43, 279.26) * mm, "end": v(-126.94, 284.67) * mm});
            skLineSegment(sketch, "E4.58.0", {"start": v(-144.56, 276.14) * mm, "end": v(-150.68, 287.27) * mm});
            skLineSegment(sketch, "E4.58.1", {"start": v(-155.7, 270.02) * mm, "end": v(-161.8, 281.15) * mm});
            skLineSegment(sketch, "E4.58.2", {"start": v(-161.8, 281.15) * mm, "end": v(-150.68, 287.27) * mm});
            skLineSegment(sketch, "E4.58.3", {"start": v(-155.7, 270.02) * mm, "end": v(-144.56, 276.14) * mm});
            skLineSegment(sketch, "E4.59.0", {"start": v(-161.61, 266.52) * mm, "end": v(-168.42, 277.24) * mm});
            skLineSegment(sketch, "E4.59.1", {"start": v(-172.34, 259.71) * mm, "end": v(-179.14, 270.43) * mm});
            skLineSegment(sketch, "E4.59.2", {"start": v(-179.14, 270.43) * mm, "end": v(-168.42, 277.24) * mm});
            skLineSegment(sketch, "E4.59.3", {"start": v(-172.34, 259.71) * mm, "end": v(-161.61, 266.52) * mm});
            skLineSegment(sketch, "E4.60.0", {"start": v(-178.03, 255.84) * mm, "end": v(-185.5, 266.12) * mm});
            skLineSegment(sketch, "E4.60.1", {"start": v(-188.3, 248.38) * mm, "end": v(-195.77, 258.65) * mm});
            skLineSegment(sketch, "E4.60.2", {"start": v(-195.77, 258.65) * mm, "end": v(-185.5, 266.12) * mm});
            skLineSegment(sketch, "E4.60.3", {"start": v(-188.3, 248.38) * mm, "end": v(-178.03, 255.84) * mm});
            skLineSegment(sketch, "E4.61.0", {"start": v(-193.74, 244.16) * mm, "end": v(-201.84, 253.94) * mm});
            skLineSegment(sketch, "E4.61.1", {"start": v(-203.53, 236.06) * mm, "end": v(-211.62, 245.85) * mm});
            skLineSegment(sketch, "E4.61.2", {"start": v(-211.62, 245.85) * mm, "end": v(-201.84, 253.94) * mm});
            skLineSegment(sketch, "E4.61.3", {"start": v(-203.53, 236.06) * mm, "end": v(-193.74, 244.16) * mm});
            skLineSegment(sketch, "E4.62.0", {"start": v(-208.7, 231.51) * mm, "end": v(-217.39, 240.77) * mm});
            skLineSegment(sketch, "E4.62.1", {"start": v(-217.95, 222.82) * mm, "end": v(-226.64, 232.08) * mm});
            skLineSegment(sketch, "E4.62.2", {"start": v(-226.64, 232.08) * mm, "end": v(-217.39, 240.77) * mm});
            skLineSegment(sketch, "E4.62.3", {"start": v(-217.95, 222.82) * mm, "end": v(-208.7, 231.51) * mm});
            skLineSegment(sketch, "E4.63.0", {"start": v(-222.82, 217.95) * mm, "end": v(-232.08, 226.64) * mm});
            skLineSegment(sketch, "E4.63.1", {"start": v(-231.51, 208.7) * mm, "end": v(-240.77, 217.39) * mm});
            skLineSegment(sketch, "E4.63.2", {"start": v(-240.77, 217.39) * mm, "end": v(-232.08, 226.64) * mm});
            skLineSegment(sketch, "E4.63.3", {"start": v(-231.51, 208.7) * mm, "end": v(-222.82, 217.95) * mm});
            skLineSegment(sketch, "E4.64.0", {"start": v(-236.06, 203.53) * mm, "end": v(-245.85, 211.62) * mm});
            skLineSegment(sketch, "E4.64.1", {"start": v(-244.16, 193.74) * mm, "end": v(-253.94, 201.84) * mm});
            skLineSegment(sketch, "E4.64.2", {"start": v(-253.94, 201.84) * mm, "end": v(-245.85, 211.62) * mm});
            skLineSegment(sketch, "E4.64.3", {"start": v(-244.16, 193.74) * mm, "end": v(-236.06, 203.53) * mm});
            skLineSegment(sketch, "E4.65.0", {"start": v(-248.38, 188.3) * mm, "end": v(-258.65, 195.77) * mm});
            skLineSegment(sketch, "E4.65.1", {"start": v(-255.84, 178.03) * mm, "end": v(-266.12, 185.5) * mm});
            skLineSegment(sketch, "E4.65.2", {"start": v(-266.12, 185.5) * mm, "end": v(-258.65, 195.77) * mm});
            skLineSegment(sketch, "E4.65.3", {"start": v(-255.84, 178.03) * mm, "end": v(-248.38, 188.3) * mm});
            skLineSegment(sketch, "E4.66.0", {"start": v(-259.71, 172.34) * mm, "end": v(-270.43, 179.14) * mm});
            skLineSegment(sketch, "E4.66.1", {"start": v(-266.52, 161.61) * mm, "end": v(-277.24, 168.42) * mm});
            skLineSegment(sketch, "E4.66.2", {"start": v(-277.24, 168.42) * mm, "end": v(-270.43, 179.14) * mm});
            skLineSegment(sketch, "E4.66.3", {"start": v(-266.52, 161.61) * mm, "end": v(-259.71, 172.34) * mm});
            skLineSegment(sketch, "E4.67.0", {"start": v(-270.02, 155.7) * mm, "end": v(-281.15, 161.8) * mm});
            skLineSegment(sketch, "E4.67.1", {"start": v(-276.14, 144.56) * mm, "end": v(-287.27, 150.68) * mm});
            skLineSegment(sketch, "E4.67.2", {"start": v(-287.27, 150.68) * mm, "end": v(-281.15, 161.8) * mm});
            skLineSegment(sketch, "E4.67.3", {"start": v(-276.14, 144.56) * mm, "end": v(-270.02, 155.7) * mm});
            skLineSegment(sketch, "E4.68.0", {"start": v(-279.26, 138.43) * mm, "end": v(-290.75, 143.84) * mm});
            skLineSegment(sketch, "E4.68.1", {"start": v(-284.67, 126.94) * mm, "end": v(-296.16, 132.34) * mm});
            skLineSegment(sketch, "E4.68.2", {"start": v(-296.16, 132.34) * mm, "end": v(-290.75, 143.84) * mm});
            skLineSegment(sketch, "E4.68.3", {"start": v(-284.67, 126.94) * mm, "end": v(-279.26, 138.43) * mm});
            skLineSegment(sketch, "E4.69.0", {"start": v(-287.4, 120.62) * mm, "end": v(-299.21, 125.3) * mm});
            skLineSegment(sketch, "E4.69.1", {"start": v(-292.08, 108.81) * mm, "end": v(-303.89, 113.49) * mm});
            skLineSegment(sketch, "E4.69.2", {"start": v(-303.89, 113.49) * mm, "end": v(-299.21, 125.3) * mm});
            skLineSegment(sketch, "E4.69.3", {"start": v(-292.08, 108.81) * mm, "end": v(-287.4, 120.62) * mm});
            skLineSegment(sketch, "E4.70.0", {"start": v(-294.4, 102.34) * mm, "end": v(-306.49, 106.26) * mm});
            skLineSegment(sketch, "E4.70.1", {"start": v(-298.33, 90.26) * mm, "end": v(-310.41, 94.18) * mm});
            skLineSegment(sketch, "E4.70.2", {"start": v(-310.41, 94.18) * mm, "end": v(-306.49, 106.26) * mm});
            skLineSegment(sketch, "E4.70.3", {"start": v(-298.33, 90.26) * mm, "end": v(-294.4, 102.34) * mm});
            skLineSegment(sketch, "E4.71.0", {"start": v(-300.25, 83.65) * mm, "end": v(-312.56, 86.8) * mm});
            skLineSegment(sketch, "E4.71.1", {"start": v(-303.41, 71.35) * mm, "end": v(-315.71, 74.5) * mm});
            skLineSegment(sketch, "E4.71.2", {"start": v(-315.71, 74.5) * mm, "end": v(-312.56, 86.8) * mm});
            skLineSegment(sketch, "E4.71.3", {"start": v(-303.41, 71.35) * mm, "end": v(-300.25, 83.65) * mm});
            skLineSegment(sketch, "E4.72.0", {"start": v(-304.91, 64.63) * mm, "end": v(-317.39, 67) * mm});
            skLineSegment(sketch, "E4.72.1", {"start": v(-307.3, 52.15) * mm, "end": v(-319.77, 54.53) * mm});
            skLineSegment(sketch, "E4.72.2", {"start": v(-319.77, 54.53) * mm, "end": v(-317.39, 67) * mm});
            skLineSegment(sketch, "E4.72.3", {"start": v(-307.3, 52.15) * mm, "end": v(-304.91, 64.63) * mm});
            skLineSegment(sketch, "E4.73.0", {"start": v(-308.37, 45.36) * mm, "end": v(-320.97, 46.95) * mm});
            skLineSegment(sketch, "E4.73.1", {"start": v(-309.96, 32.76) * mm, "end": v(-322.56, 34.35) * mm});
            skLineSegment(sketch, "E4.73.2", {"start": v(-322.56, 34.35) * mm, "end": v(-320.97, 46.95) * mm});
            skLineSegment(sketch, "E4.73.3", {"start": v(-309.96, 32.76) * mm, "end": v(-308.37, 45.36) * mm});
            skLineSegment(sketch, "E4.74.0", {"start": v(-310.61, 25.9) * mm, "end": v(-323.29, 26.7) * mm});
            skLineSegment(sketch, "E4.74.1", {"start": v(-311.4, 13.23) * mm, "end": v(-324.08, 14.03) * mm});
            skLineSegment(sketch, "E4.74.2", {"start": v(-324.08, 14.03) * mm, "end": v(-323.29, 26.7) * mm});
            skLineSegment(sketch, "E4.74.3", {"start": v(-311.4, 13.23) * mm, "end": v(-310.61, 25.9) * mm});
            skLineSegment(sketch, "E4.75.0", {"start": v(-311.62, 6.35) * mm, "end": v(-324.32, 6.35) * mm});
            skLineSegment(sketch, "E4.75.1", {"start": v(-311.62, -6.35) * mm, "end": v(-324.32, -6.35) * mm});
            skLineSegment(sketch, "E4.75.2", {"start": v(-324.32, -6.35) * mm, "end": v(-324.32, 6.35) * mm});
            skLineSegment(sketch, "E4.75.3", {"start": v(-311.62, -6.35) * mm, "end": v(-311.62, 6.35) * mm});
            skLineSegment(sketch, "E4.76.0", {"start": v(-311.4, -13.23) * mm, "end": v(-324.08, -14.03) * mm});
            skLineSegment(sketch, "E4.76.1", {"start": v(-310.61, -25.9) * mm, "end": v(-323.29, -26.7) * mm});
            skLineSegment(sketch, "E4.76.2", {"start": v(-323.29, -26.7) * mm, "end": v(-324.08, -14.03) * mm});
            skLineSegment(sketch, "E4.76.3", {"start": v(-310.61, -25.9) * mm, "end": v(-311.4, -13.23) * mm});
            skLineSegment(sketch, "E4.77.0", {"start": v(-309.96, -32.76) * mm, "end": v(-322.56, -34.35) * mm});
            skLineSegment(sketch, "E4.77.1", {"start": v(-308.37, -45.36) * mm, "end": v(-320.97, -46.95) * mm});
            skLineSegment(sketch, "E4.77.2", {"start": v(-320.97, -46.95) * mm, "end": v(-322.56, -34.35) * mm});
            skLineSegment(sketch, "E4.77.3", {"start": v(-308.37, -45.36) * mm, "end": v(-309.96, -32.76) * mm});
            skLineSegment(sketch, "E4.78.0", {"start": v(-307.3, -52.15) * mm, "end": v(-319.77, -54.53) * mm});
            skLineSegment(sketch, "E4.78.1", {"start": v(-304.91, -64.63) * mm, "end": v(-317.39, -67) * mm});
            skLineSegment(sketch, "E4.78.2", {"start": v(-317.39, -67) * mm, "end": v(-319.77, -54.53) * mm});
            skLineSegment(sketch, "E4.78.3", {"start": v(-304.91, -64.63) * mm, "end": v(-307.3, -52.15) * mm});
            skLineSegment(sketch, "E4.79.0", {"start": v(-303.41, -71.35) * mm, "end": v(-315.71, -74.5) * mm});
            skLineSegment(sketch, "E4.79.1", {"start": v(-300.25, -83.65) * mm, "end": v(-312.56, -86.8) * mm});
            skLineSegment(sketch, "E4.79.2", {"start": v(-312.56, -86.8) * mm, "end": v(-315.71, -74.5) * mm});
            skLineSegment(sketch, "E4.79.3", {"start": v(-300.25, -83.65) * mm, "end": v(-303.41, -71.35) * mm});
            skLineSegment(sketch, "E4.80.0", {"start": v(-298.33, -90.26) * mm, "end": v(-310.41, -94.18) * mm});
            skLineSegment(sketch, "E4.80.1", {"start": v(-294.4, -102.34) * mm, "end": v(-306.49, -106.26) * mm});
            skLineSegment(sketch, "E4.80.2", {"start": v(-306.49, -106.26) * mm, "end": v(-310.41, -94.18) * mm});
            skLineSegment(sketch, "E4.80.3", {"start": v(-294.4, -102.34) * mm, "end": v(-298.33, -90.26) * mm});
            skLineSegment(sketch, "E4.81.0", {"start": v(-292.08, -108.81) * mm, "end": v(-303.89, -113.49) * mm});
            skLineSegment(sketch, "E4.81.1", {"start": v(-287.4, -120.62) * mm, "end": v(-299.21, -125.3) * mm});
            skLineSegment(sketch, "E4.81.2", {"start": v(-299.21, -125.3) * mm, "end": v(-303.89, -113.49) * mm});
            skLineSegment(sketch, "E4.81.3", {"start": v(-287.4, -120.62) * mm, "end": v(-292.08, -108.81) * mm});
            skLineSegment(sketch, "E4.82.0", {"start": v(-284.67, -126.94) * mm, "end": v(-296.16, -132.34) * mm});
            skLineSegment(sketch, "E4.82.1", {"start": v(-279.26, -138.43) * mm, "end": v(-290.75, -143.84) * mm});
            skLineSegment(sketch, "E4.82.2", {"start": v(-290.75, -143.84) * mm, "end": v(-296.16, -132.34) * mm});
            skLineSegment(sketch, "E4.82.3", {"start": v(-279.26, -138.43) * mm, "end": v(-284.67, -126.94) * mm});
            skLineSegment(sketch, "E4.83.0", {"start": v(-276.14, -144.56) * mm, "end": v(-287.27, -150.68) * mm});
            skLineSegment(sketch, "E4.83.1", {"start": v(-270.02, -155.7) * mm, "end": v(-281.15, -161.8) * mm});
            skLineSegment(sketch, "E4.83.2", {"start": v(-281.15, -161.8) * mm, "end": v(-287.27, -150.68) * mm});
            skLineSegment(sketch, "E4.83.3", {"start": v(-270.02, -155.7) * mm, "end": v(-276.14, -144.56) * mm});
            skLineSegment(sketch, "E4.84.0", {"start": v(-266.52, -161.61) * mm, "end": v(-277.24, -168.42) * mm});
            skLineSegment(sketch, "E4.84.1", {"start": v(-259.71, -172.34) * mm, "end": v(-270.43, -179.14) * mm});
            skLineSegment(sketch, "E4.84.2", {"start": v(-270.43, -179.14) * mm, "end": v(-277.24, -168.42) * mm});
            skLineSegment(sketch, "E4.84.3", {"start": v(-259.71, -172.34) * mm, "end": v(-266.52, -161.61) * mm});
            skLineSegment(sketch, "E4.85.0", {"start": v(-255.84, -178.03) * mm, "end": v(-266.12, -185.5) * mm});
            skLineSegment(sketch, "E4.85.1", {"start": v(-248.38, -188.3) * mm, "end": v(-258.65, -195.77) * mm});
            skLineSegment(sketch, "E4.85.2", {"start": v(-258.65, -195.77) * mm, "end": v(-266.12, -185.5) * mm});
            skLineSegment(sketch, "E4.85.3", {"start": v(-248.38, -188.3) * mm, "end": v(-255.84, -178.03) * mm});
            skLineSegment(sketch, "E4.86.0", {"start": v(-244.16, -193.74) * mm, "end": v(-253.94, -201.84) * mm});
            skLineSegment(sketch, "E4.86.1", {"start": v(-236.06, -203.53) * mm, "end": v(-245.85, -211.62) * mm});
            skLineSegment(sketch, "E4.86.2", {"start": v(-245.85, -211.62) * mm, "end": v(-253.94, -201.84) * mm});
            skLineSegment(sketch, "E4.86.3", {"start": v(-236.06, -203.53) * mm, "end": v(-244.16, -193.74) * mm});
            skLineSegment(sketch, "E4.87.0", {"start": v(-231.51, -208.7) * mm, "end": v(-240.77, -217.39) * mm});
            skLineSegment(sketch, "E4.87.1", {"start": v(-222.82, -217.95) * mm, "end": v(-232.08, -226.64) * mm});
            skLineSegment(sketch, "E4.87.2", {"start": v(-232.08, -226.64) * mm, "end": v(-240.77, -217.39) * mm});
            skLineSegment(sketch, "E4.87.3", {"start": v(-222.82, -217.95) * mm, "end": v(-231.51, -208.7) * mm});
            skLineSegment(sketch, "E4.88.0", {"start": v(-217.95, -222.82) * mm, "end": v(-226.64, -232.08) * mm});
            skLineSegment(sketch, "E4.88.1", {"start": v(-208.7, -231.51) * mm, "end": v(-217.39, -240.77) * mm});
            skLineSegment(sketch, "E4.88.2", {"start": v(-217.39, -240.77) * mm, "end": v(-226.64, -232.08) * mm});
            skLineSegment(sketch, "E4.88.3", {"start": v(-208.7, -231.51) * mm, "end": v(-217.95, -222.82) * mm});
            skLineSegment(sketch, "E4.89.0", {"start": v(-203.53, -236.06) * mm, "end": v(-211.62, -245.85) * mm});
            skLineSegment(sketch, "E4.89.1", {"start": v(-193.74, -244.16) * mm, "end": v(-201.84, -253.94) * mm});
            skLineSegment(sketch, "E4.89.2", {"start": v(-201.84, -253.94) * mm, "end": v(-211.62, -245.85) * mm});
            skLineSegment(sketch, "E4.89.3", {"start": v(-193.74, -244.16) * mm, "end": v(-203.53, -236.06) * mm});
            skLineSegment(sketch, "E4.90.0", {"start": v(-188.3, -248.38) * mm, "end": v(-195.77, -258.65) * mm});
            skLineSegment(sketch, "E4.90.1", {"start": v(-178.03, -255.84) * mm, "end": v(-185.5, -266.12) * mm});
            skLineSegment(sketch, "E4.90.2", {"start": v(-185.5, -266.12) * mm, "end": v(-195.77, -258.65) * mm});
            skLineSegment(sketch, "E4.90.3", {"start": v(-178.03, -255.84) * mm, "end": v(-188.3, -248.38) * mm});
            skLineSegment(sketch, "E4.91.0", {"start": v(-172.34, -259.71) * mm, "end": v(-179.14, -270.43) * mm});
            skLineSegment(sketch, "E4.91.1", {"start": v(-161.61, -266.52) * mm, "end": v(-168.42, -277.24) * mm});
            skLineSegment(sketch, "E4.91.2", {"start": v(-168.42, -277.24) * mm, "end": v(-179.14, -270.43) * mm});
            skLineSegment(sketch, "E4.91.3", {"start": v(-161.61, -266.52) * mm, "end": v(-172.34, -259.71) * mm});
            skLineSegment(sketch, "E4.92.0", {"start": v(-155.7, -270.02) * mm, "end": v(-161.8, -281.15) * mm});
            skLineSegment(sketch, "E4.92.1", {"start": v(-144.56, -276.14) * mm, "end": v(-150.68, -287.27) * mm});
            skLineSegment(sketch, "E4.92.2", {"start": v(-150.68, -287.27) * mm, "end": v(-161.8, -281.15) * mm});
            skLineSegment(sketch, "E4.92.3", {"start": v(-144.56, -276.14) * mm, "end": v(-155.7, -270.02) * mm});
            skLineSegment(sketch, "E4.93.0", {"start": v(-138.43, -279.26) * mm, "end": v(-143.84, -290.75) * mm});
            skLineSegment(sketch, "E4.93.1", {"start": v(-126.94, -284.67) * mm, "end": v(-132.34, -296.16) * mm});
            skLineSegment(sketch, "E4.93.2", {"start": v(-132.34, -296.16) * mm, "end": v(-143.84, -290.75) * mm});
            skLineSegment(sketch, "E4.93.3", {"start": v(-126.94, -284.67) * mm, "end": v(-138.43, -279.26) * mm});
            skLineSegment(sketch, "E4.94.0", {"start": v(-120.62, -287.4) * mm, "end": v(-125.3, -299.21) * mm});
            skLineSegment(sketch, "E4.94.1", {"start": v(-108.81, -292.08) * mm, "end": v(-113.49, -303.89) * mm});
            skLineSegment(sketch, "E4.94.2", {"start": v(-113.49, -303.89) * mm, "end": v(-125.3, -299.21) * mm});
            skLineSegment(sketch, "E4.94.3", {"start": v(-108.81, -292.08) * mm, "end": v(-120.62, -287.4) * mm});
            skLineSegment(sketch, "E4.95.0", {"start": v(-102.34, -294.4) * mm, "end": v(-106.26, -306.49) * mm});
            skLineSegment(sketch, "E4.95.1", {"start": v(-90.26, -298.33) * mm, "end": v(-94.18, -310.41) * mm});
            skLineSegment(sketch, "E4.95.2", {"start": v(-94.18, -310.41) * mm, "end": v(-106.26, -306.49) * mm});
            skLineSegment(sketch, "E4.95.3", {"start": v(-90.26, -298.33) * mm, "end": v(-102.34, -294.4) * mm});
            skLineSegment(sketch, "E4.96.0", {"start": v(-83.65, -300.25) * mm, "end": v(-86.8, -312.56) * mm});
            skLineSegment(sketch, "E4.96.1", {"start": v(-71.35, -303.41) * mm, "end": v(-74.5, -315.71) * mm});
            skLineSegment(sketch, "E4.96.2", {"start": v(-74.5, -315.71) * mm, "end": v(-86.8, -312.56) * mm});
            skLineSegment(sketch, "E4.96.3", {"start": v(-71.35, -303.41) * mm, "end": v(-83.65, -300.25) * mm});
            skLineSegment(sketch, "E4.97.0", {"start": v(-64.63, -304.91) * mm, "end": v(-67, -317.39) * mm});
            skLineSegment(sketch, "E4.97.1", {"start": v(-52.15, -307.3) * mm, "end": v(-54.53, -319.77) * mm});
            skLineSegment(sketch, "E4.97.2", {"start": v(-54.53, -319.77) * mm, "end": v(-67, -317.39) * mm});
            skLineSegment(sketch, "E4.97.3", {"start": v(-52.15, -307.3) * mm, "end": v(-64.63, -304.91) * mm});
            skLineSegment(sketch, "E4.98.0", {"start": v(-45.36, -308.37) * mm, "end": v(-46.95, -320.97) * mm});
            skLineSegment(sketch, "E4.98.1", {"start": v(-32.76, -309.96) * mm, "end": v(-34.35, -322.56) * mm});
            skLineSegment(sketch, "E4.98.2", {"start": v(-34.35, -322.56) * mm, "end": v(-46.95, -320.97) * mm});
            skLineSegment(sketch, "E4.98.3", {"start": v(-32.76, -309.96) * mm, "end": v(-45.36, -308.37) * mm});
            skLineSegment(sketch, "E4.99.0", {"start": v(-25.9, -310.61) * mm, "end": v(-26.7, -323.29) * mm});
            skLineSegment(sketch, "E4.99.1", {"start": v(-13.23, -311.4) * mm, "end": v(-14.03, -324.08) * mm});
            skLineSegment(sketch, "E4.99.2", {"start": v(-14.03, -324.08) * mm, "end": v(-26.7, -323.29) * mm});
            skLineSegment(sketch, "E4.99.3", {"start": v(-13.23, -311.4) * mm, "end": v(-25.9, -310.61) * mm});
            skPoint(sketch, "E4.center", {"position": v(0, 0) * mm});
            skSolve(sketch);
        }
        {
            var Q0;
            Q0 = qSketchRegion(id + "F7", true);
            extrude(context, id + "F8", {"entities" : qUnion([Q0]), "operationType" : NewBodyOperationType.ADD, "depth" : 203.2 * mm});
        }
        {
            var Q0;
            Q0=qCreatedBy(makeId("Right.planeOp"),FACE);
            var sketch = newSketch(context, id + "F9", { "sketchPlane" : qUnion([Q0])});
            skLineSegment(sketch, "E5.bottom", {"start": v(316.02, 12.83) * mm, "end": v(328.72, 12.83) * mm});
            skLineSegment(sketch, "E5.top", {"start": v(316.02, 25.53) * mm, "end": v(328.72, 25.53) * mm});
            skLineSegment(sketch, "E5.left", {"start": v(316.02, 12.83) * mm, "end": v(316.02, 25.53) * mm});
            skLineSegment(sketch, "E5.right", {"start": v(328.72, 12.83) * mm, "end": v(328.72, 25.53) * mm});
            skPoint(sketch, "E5.middle", {"position": v(322.37, 19.18) * mm});
            skLineSegment(sketch, "E6.0.1.0", {"start": v(316.02, 45.34) * mm, "end": v(328.72, 45.34) * mm});
            skLineSegment(sketch, "E6.0.1.1", {"start": v(328.72, 45.34) * mm, "end": v(328.72, 58.04) * mm});
            skLineSegment(sketch, "E6.0.1.2", {"start": v(316.02, 58.04) * mm, "end": v(328.72, 58.04) * mm});
            skLineSegment(sketch, "E6.0.1.3", {"start": v(316.02, 45.34) * mm, "end": v(316.02, 58.04) * mm});
            skLineSegment(sketch, "E6.0.2.0", {"start": v(316.02, 77.86) * mm, "end": v(328.72, 77.86) * mm});
            skLineSegment(sketch, "E6.0.2.1", {"start": v(328.72, 77.86) * mm, "end": v(328.72, 90.56) * mm});
            skLineSegment(sketch, "E6.0.2.2", {"start": v(316.02, 90.56) * mm, "end": v(328.72, 90.56) * mm});
            skLineSegment(sketch, "E6.0.2.3", {"start": v(316.02, 77.86) * mm, "end": v(316.02, 90.56) * mm});
            skLineSegment(sketch, "E6.0.3.0", {"start": v(316.02, 110.37) * mm, "end": v(328.72, 110.37) * mm});
            skLineSegment(sketch, "E6.0.3.1", {"start": v(328.72, 110.37) * mm, "end": v(328.72, 123.07) * mm});
            skLineSegment(sketch, "E6.0.3.2", {"start": v(316.02, 123.07) * mm, "end": v(328.72, 123.07) * mm});
            skLineSegment(sketch, "E6.0.3.3", {"start": v(316.02, 110.37) * mm, "end": v(316.02, 123.07) * mm});
            skLineSegment(sketch, "E6.0.4.0", {"start": v(316.02, 142.88) * mm, "end": v(328.72, 142.88) * mm});
            skLineSegment(sketch, "E6.0.4.1", {"start": v(328.72, 142.88) * mm, "end": v(328.72, 155.58) * mm});
            skLineSegment(sketch, "E6.0.4.2", {"start": v(316.02, 155.58) * mm, "end": v(328.72, 155.58) * mm});
            skLineSegment(sketch, "E6.0.4.3", {"start": v(316.02, 142.88) * mm, "end": v(316.02, 155.58) * mm});
            skLineSegment(sketch, "E6.0.5.0", {"start": v(316.02, 175.4) * mm, "end": v(328.72, 175.4) * mm});
            skLineSegment(sketch, "E6.0.5.1", {"start": v(328.72, 175.4) * mm, "end": v(328.72, 188.1) * mm});
            skLineSegment(sketch, "E6.0.5.2", {"start": v(316.02, 188.1) * mm, "end": v(328.72, 188.1) * mm});
            skLineSegment(sketch, "E6.0.5.3", {"start": v(316.02, 175.4) * mm, "end": v(316.02, 188.1) * mm});
            skLineSegment(sketch, "E6.direction1", {"start": v(316.02, 12.83) * mm, "end": v(341.42, 12.83) * mm, "construction": true});
            skLineSegment(sketch, "E6.direction2", {"start": v(316.02, 12.83) * mm, "end": v(316.02, 45.34) * mm, "construction": true});
            skSolve(sketch);
        }
        {
            var Q0;
            Q0=makeQuery(id+"F9.imprint","IMPRINT",FACE,{"disambiguationData":[TD([[makeQuery(id+"F9.imprint","IMPRINT",EDGE,{"derivedFrom":sQuery(id+"F9.wireOp",EDGE,"E6.0.5.0")}),1.0]])]});
            var Q1;
            Q1=makeQuery(id+"F9.imprint","IMPRINT",FACE,{"disambiguationData":[TD([[makeQuery(id+"F9.imprint","IMPRINT",EDGE,{"derivedFrom":sQuery(id+"F9.wireOp",EDGE,"E6.0.4.0")}),1.0]])]});
            var Q2;
            Q2=makeQuery(id+"F9.imprint","IMPRINT",FACE,{"disambiguationData":[TD([[makeQuery(id+"F9.imprint","IMPRINT",EDGE,{"derivedFrom":sQuery(id+"F9.wireOp",EDGE,"E6.0.3.0")}),1.0]])]});
            var Q3;
            Q3=makeQuery(id+"F9.imprint","IMPRINT",FACE,{"disambiguationData":[TD([[makeQuery(id+"F9.imprint","IMPRINT",EDGE,{"derivedFrom":sQuery(id+"F9.wireOp",EDGE,"E6.0.2.0")}),1.0]])]});
            var Q4;
            Q4=makeQuery(id+"F9.imprint","IMPRINT",FACE,{"disambiguationData":[TD([[makeQuery(id+"F9.imprint","IMPRINT",EDGE,{"derivedFrom":sQuery(id+"F9.wireOp",EDGE,"E6.0.1.0")}),1.0]])]});
            var Q5;
            Q5=makeQuery(id+"F9.imprint","IMPRINT",FACE,{"disambiguationData":[TD([[makeQuery(id+"F9.imprint","IMPRINT",EDGE,{"derivedFrom":sQuery(id+"F9.wireOp",EDGE,"E5.bottom")}),1.0]])]});
            var Q6;
            {var subQ0=sQuery(id+"F0.wireOp",EDGE,"E0");Q6=makeQuery(id+"F6.opFillet","BLEND_EDGE",EDGE,{"blendedFrom":[makeQuery(id+"F2.opChamfer","BLEND_EDGE",EDGE,{"blendedFrom":[makeQuery(id+"F1.opExtrude","CAP_EDGE",EDGE,{"disambiguationData":[OSD([subQ0])],"isStart":true}),makeQuery(id+"F1.opExtrude","SWEPT_FACE",FACE,{"disambiguationData":[OSD([subQ0])]})],"blendedInto":[makeQuery(id+"F1.opExtrude","SWEPT_FACE",FACE,{"disambiguationData":[OSD([subQ0])]})]}),makeQuery(id+"F2.opChamfer","BLEND_FACE",FACE,{"disambiguationData":[OSD([subQ0])]})],"blendedInto":[makeQuery(id+"F2.opChamfer","BLEND_FACE",FACE,{"disambiguationData":[OSD([subQ0])]})]});}
            revolve(context, id + "F10", {"operationType" : NewBodyOperationType.REMOVE, "entities" : qUnion([Q0, Q1, Q2, Q3, Q4, Q5]), "axis" : qUnion([Q6]), "revolveType" : RevolveType.FULL, "oppositeDirection" : true});
        }
    });
